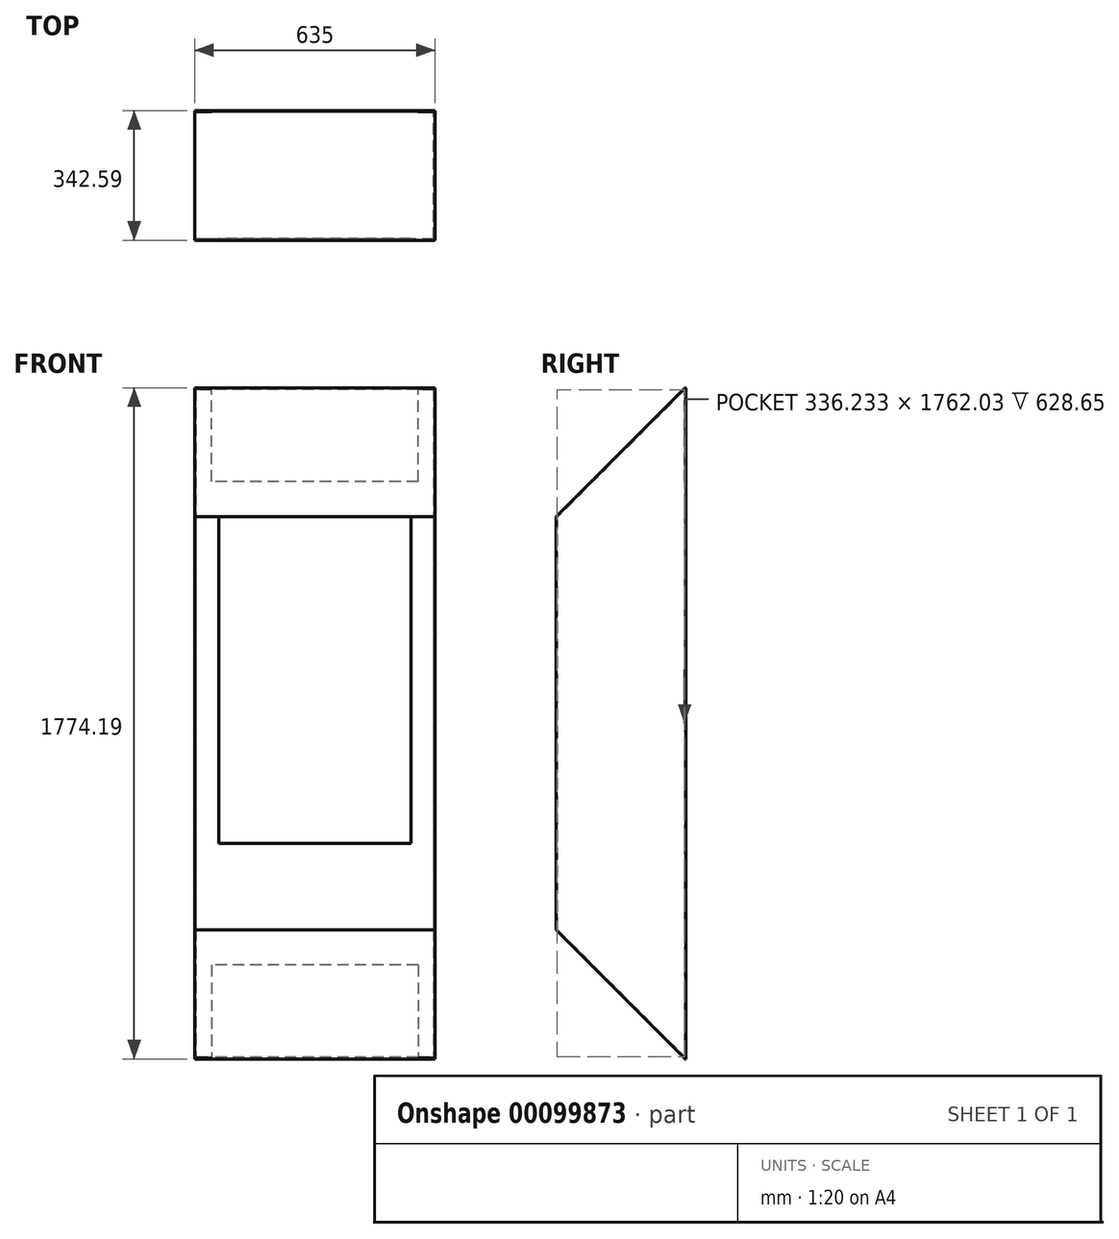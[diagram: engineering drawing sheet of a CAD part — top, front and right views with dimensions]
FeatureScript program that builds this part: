
annotation { "Feature Type Name" : "Feature", "Feature Type Description" : "" }
export const myFeature = defineFeature(function(context is Context, id is Id, definition is map)
    precondition{}
    {
        {
            var Q0;
            Q0=qCreatedBy(makeId("Right.planeOp"),FACE);
            var sketch = newSketch(context, id + "F0", { "sketchPlane" : qUnion([Q0])});
            skLineSegment(sketch, "E0", {"start": v(0, 0) * mm, "end": v(0, 1774.19) * mm});
            skLineSegment(sketch, "E1", {"start": v(0, 1774.19) * mm, "end": v(-341, 1433.2) * mm});
            skLineSegment(sketch, "E2", {"start": v(-341, 1433.2) * mm, "end": v(-341, 341) * mm});
            skLineSegment(sketch, "E3", {"start": v(-341, 341) * mm, "end": v(0, 0) * mm});
            skSolve(sketch);
        }
        {
            var Q0;
            Q0=qSketchRegion(id+"F0",true);
            extrude(context, id + "F1", {"entities" : qUnion([Q0]), "endBound" : BoundingType.SYMMETRIC, "depth" : 635 * mm});
        }
        {
            var Q0;
            Q0=makeQuery(id+"F1.opExtrude","SWEPT_FACE",FACE,{"disambiguationData":[OSD([sQuery(id+"F0.wireOp",EDGE,"E0")])]});
            shell(context, id + "F2", {"entities" : qUnion([Q0]), "thickness" : 3.17 * mm});
        }
        {
            var Q0;
            Q0=qCreatedBy(makeId("Front.planeOp"),FACE);
            var sketch = newSketch(context, id + "F3", { "sketchPlane" : qUnion([Q0])});
            skLineSegment(sketch, "E4.bottom", {"start": v(273.11, 247.9) * mm, "end": v(-273.11, 247.9) * mm});
            skLineSegment(sketch, "E4.top", {"start": v(273.11, 1526.29) * mm, "end": v(-273.11, 1526.29) * mm});
            skLineSegment(sketch, "E4.left", {"start": v(317.5, 247.9) * mm, "end": v(317.5, 1526.29) * mm});
            skLineSegment(sketch, "E4.right", {"start": v(-317.5, 247.9) * mm, "end": v(-317.5, 1526.29) * mm});
            skLineSegment(sketch, "E5.top", {"start": v(317.5, 1774.19) * mm, "end": v(273.11, 1774.19) * mm});
            skLineSegment(sketch, "E5.left", {"start": v(317.5, 1526.29) * mm, "end": v(317.5, 1774.19) * mm});
            skLineSegment(sketch, "E5.right", {"start": v(273.11, 1526.29) * mm, "end": v(273.11, 1774.19) * mm});
            skLineSegment(sketch, "E6.top", {"start": v(-317.5, 1774.19) * mm, "end": v(-273.11, 1774.19) * mm});
            skLineSegment(sketch, "E6.left", {"start": v(-317.5, 1526.29) * mm, "end": v(-317.5, 1774.19) * mm});
            skLineSegment(sketch, "E6.right", {"start": v(-273.11, 1526.29) * mm, "end": v(-273.11, 1774.19) * mm});
            skLineSegment(sketch, "E7.top", {"start": v(-317.5, 0) * mm, "end": v(-273.11, 0) * mm});
            skLineSegment(sketch, "E7.left", {"start": v(-317.5, 247.9) * mm, "end": v(-317.5, 0) * mm});
            skLineSegment(sketch, "E7.right", {"start": v(-273.11, 247.9) * mm, "end": v(-273.11, 0) * mm});
            skLineSegment(sketch, "E8.top", {"start": v(317.5, 0) * mm, "end": v(273.11, 0) * mm});
            skLineSegment(sketch, "E8.left", {"start": v(317.5, 247.9) * mm, "end": v(317.5, 0) * mm});
            skLineSegment(sketch, "E8.right", {"start": v(273.11, 247.9) * mm, "end": v(273.11, 0) * mm});
            skSolve(sketch);
        }
        {
            var Q0;
            Q0=qSketchRegion(id+"F3",true);
            extrude(context, id + "F4", {"entities" : qUnion([Q0]), "operationType" : NewBodyOperationType.ADD, "endBound" : BoundingType.SYMMETRIC, "depth" : 3.17 * mm});
        }
        {
            var Q0;
            Q0=makeQuery(id+"F1.opExtrude","SWEPT_FACE",FACE,{"disambiguationData":[OSD([sQuery(id+"F0.wireOp",EDGE,"E2")])]});
            var sketch = newSketch(context, id + "F5", { "sketchPlane" : qUnion([Q0])});
            skLineSegment(sketch, "E9.bottom", {"start": v(-254, 1433.2) * mm, "end": v(254, 1433.2) * mm});
            skLineSegment(sketch, "E9.top", {"start": v(-254, 569.6) * mm, "end": v(254, 569.6) * mm});
            skLineSegment(sketch, "E9.left", {"start": v(-254, 1433.2) * mm, "end": v(-254, 569.6) * mm});
            skLineSegment(sketch, "E9.right", {"start": v(254, 1433.2) * mm, "end": v(254, 569.6) * mm});
            skSolve(sketch);
        }
        {
            var Q0;
            Q0=qSketchRegion(id+"F5",true);
            extrude(context, id + "F6", {"entities" : qUnion([Q0]), "operationType" : NewBodyOperationType.REMOVE, "endBound" : BoundingType.UP_TO_NEXT, "oppositeDirection" : true, "depth" : 25.4 * mm});
        }
    });
